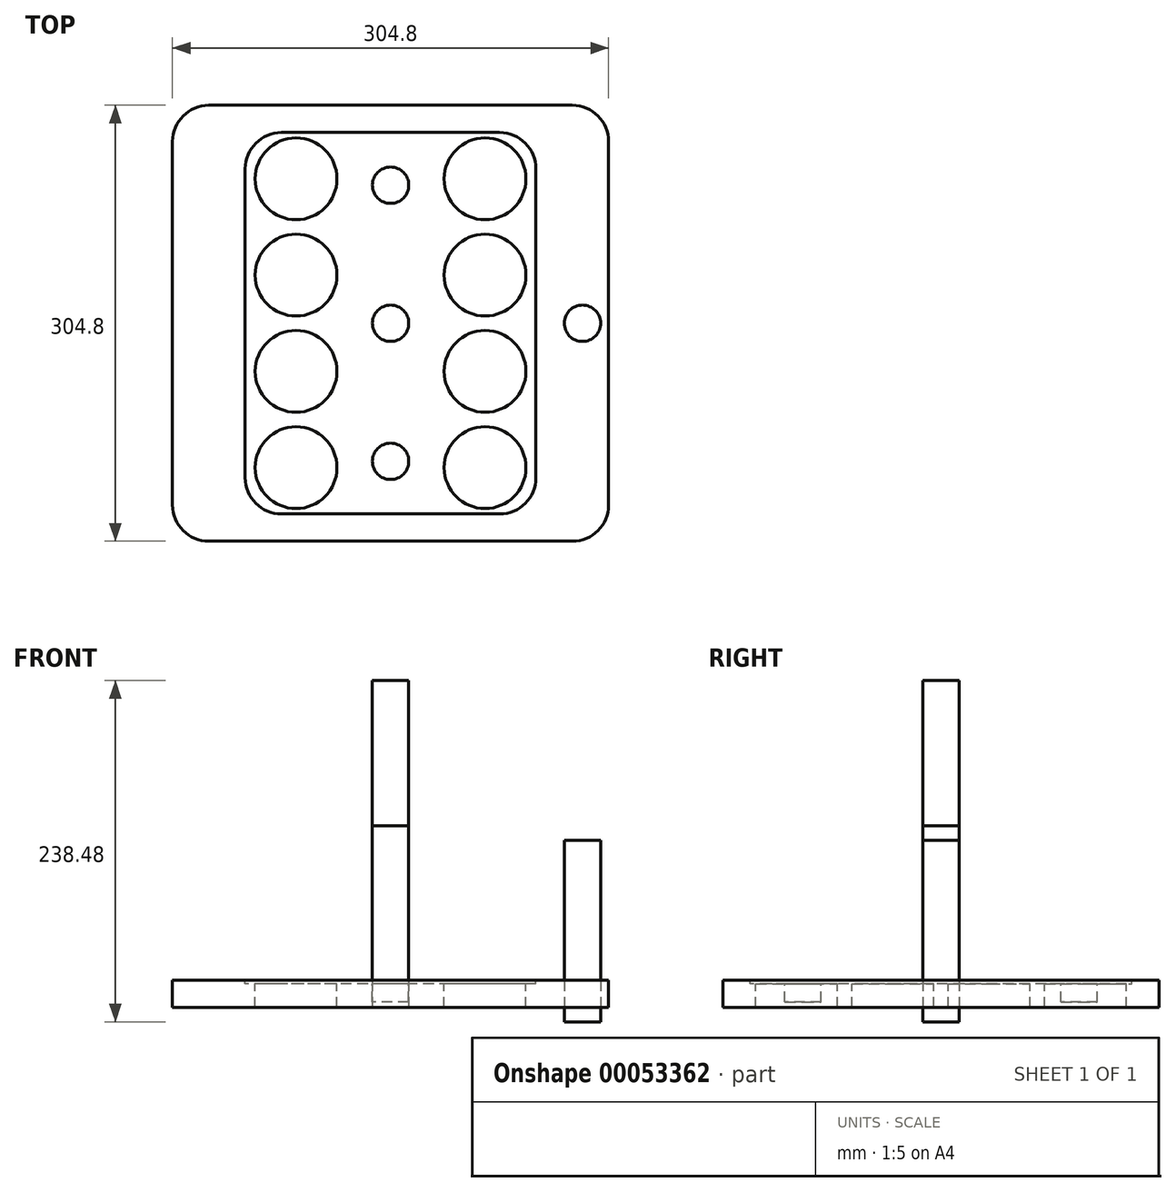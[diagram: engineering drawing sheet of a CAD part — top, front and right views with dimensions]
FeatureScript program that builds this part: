
annotation { "Feature Type Name" : "Feature", "Feature Type Description" : "" }
export const myFeature = defineFeature(function(context is Context, id is Id, definition is map)
    precondition{}
    {
        {
            var Q0;
            Q0=qCreatedBy(makeId("Top.planeOp"),FACE);
            var sketch = newSketch(context, id + "F0", { "sketchPlane" : qUnion([Q0])});
            skLineSegment(sketch, "E0.rect.bottom", {"start": v(127, 152.4) * mm, "end": v(-127, 152.4) * mm});
            skLineSegment(sketch, "E0.rect.top", {"start": v(127, -152.4) * mm, "end": v(-127, -152.4) * mm});
            skLineSegment(sketch, "E0.rect.left", {"start": v(152.4, 127) * mm, "end": v(152.4, -127) * mm});
            skLineSegment(sketch, "E0.rect.right", {"start": v(-152.4, 127) * mm, "end": v(-152.4, -127) * mm});
            skPoint(sketch, "E1.visualSharp", {"position": v(-152.4, 152.4) * mm});
            skArc(sketch, "E1.filletArc", {"start": v(-127, 152.4) * mm, "mid": v(-144.96, 144.96) * mm, "end": v(-152.4, 127) * mm});
            skPoint(sketch, "E2.visualSharp", {"position": v(152.4, 152.4) * mm});
            skArc(sketch, "E2.filletArc", {"start": v(152.4, 127) * mm, "mid": v(144.96, 144.96) * mm, "end": v(127, 152.4) * mm});
            skPoint(sketch, "E3.visualSharp", {"position": v(152.4, -152.4) * mm});
            skArc(sketch, "E3.filletArc", {"start": v(127, -152.4) * mm, "mid": v(144.96, -144.96) * mm, "end": v(152.4, -127) * mm});
            skPoint(sketch, "E4.visualSharp", {"position": v(-152.4, -152.4) * mm});
            skArc(sketch, "E4.filletArc", {"start": v(-152.4, -127) * mm, "mid": v(-144.96, -144.96) * mm, "end": v(-127, -152.4) * mm});
            skSolve(sketch);
        }
        {
            var Q0;
            Q0=qSketchRegion(id+"F0",true);
            extrude(context, id + "F1", {"entities" : qUnion([Q0]), "depth" : 19.05 * mm});
        }
        {
            var Q0;
            Q0=makeQuery(id+"F1.opExtrude","CAP_FACE",FACE,{"disambiguationData":[OSD([sQuery(id+"F0.wireOp",EDGE,"E0.rect.bottom"),sQuery(id+"F0.wireOp",EDGE,"E0.rect.top"),sQuery(id+"F0.wireOp",EDGE,"E0.rect.left"),sQuery(id+"F0.wireOp",EDGE,"E0.rect.right"),sQuery(id+"F0.wireOp",EDGE,"E1.filletArc"),sQuery(id+"F0.wireOp",EDGE,"E2.filletArc"),sQuery(id+"F0.wireOp",EDGE,"E3.filletArc"),sQuery(id+"F0.wireOp",EDGE,"E4.filletArc")])],"isStart":false});
            var sketch = newSketch(context, id + "F2", { "sketchPlane" : qUnion([Q0])});
            skCircle(sketch, "E5", {"center": v(-66.04, 100.96) * mm, "radius": 28.58 * mm});
            skCircle(sketch, "E6", {"center": v(-66.04, 33.65) * mm, "radius": 28.58 * mm});
            skCircle(sketch, "E7", {"center": v(-66.04, -33.66) * mm, "radius": 28.58 * mm});
            skCircle(sketch, "E8", {"center": v(-66.04, -100.97) * mm, "radius": 28.58 * mm});
            skLineSegment(sketch, "E9", {"start": v(-211.39, 0) * mm, "end": v(197.24, 0) * mm, "construction": true});
            skPoint(sketch, "E9.endSnap0", {"position": v(-152.4, 0) * mm});
            skCircle(sketch, "E10.MirrorC", {"center": v(66.04, -100.97) * mm, "radius": 28.58 * mm});
            skCircle(sketch, "E11.MirrorC", {"center": v(66.04, -33.66) * mm, "radius": 28.58 * mm});
            skCircle(sketch, "E12.MirrorC", {"center": v(66.04, 33.65) * mm, "radius": 28.58 * mm});
            skCircle(sketch, "E13.MirrorC", {"center": v(66.04, 100.96) * mm, "radius": 28.58 * mm});
            skSolve(sketch);
        }
        {
            var Q0;
            Q0=qSketchRegion(id+"F2",true);
            extrude(context, id + "F3", {"entities" : qUnion([Q0]), "operationType" : NewBodyOperationType.REMOVE, "endBound" : BoundingType.THROUGH_ALL, "oppositeDirection" : true, "depth" : 25.4 * mm});
        }
        {
            var Q0;
            Q0=makeQuery(id+"F1.opExtrude","CAP_FACE",FACE,{"disambiguationData":[OSD([sQuery(id+"F0.wireOp",EDGE,"E0.rect.bottom"),sQuery(id+"F0.wireOp",EDGE,"E0.rect.top"),sQuery(id+"F0.wireOp",EDGE,"E0.rect.left"),sQuery(id+"F0.wireOp",EDGE,"E0.rect.right"),sQuery(id+"F0.wireOp",EDGE,"E1.filletArc"),sQuery(id+"F0.wireOp",EDGE,"E2.filletArc"),sQuery(id+"F0.wireOp",EDGE,"E3.filletArc"),sQuery(id+"F0.wireOp",EDGE,"E4.filletArc")])],"isStart":false});
            var sketch = newSketch(context, id + "F4", { "sketchPlane" : qUnion([Q0])});
            skCircle(sketch, "E14", {"center": v(0, 96.52) * mm, "radius": 12.7 * mm});
            skCircle(sketch, "E15.MirrorC", {"center": v(0, -96.52) * mm, "radius": 12.7 * mm});
            skSolve(sketch);
        }
        {
            var Q0;
            Q0=qSketchRegion(id+"F4",true);
            extrude(context, id + "F5", {"entities" : qUnion([Q0]), "operationType" : NewBodyOperationType.REMOVE, "oppositeDirection" : true, "depth" : 15.24 * mm});
        }
        {
            var Q0;
            Q0=makeQuery(id+"F1.opExtrude","CAP_FACE",FACE,{"disambiguationData":[OSD([sQuery(id+"F0.wireOp",EDGE,"E0.rect.bottom"),sQuery(id+"F0.wireOp",EDGE,"E0.rect.top"),sQuery(id+"F0.wireOp",EDGE,"E0.rect.left"),sQuery(id+"F0.wireOp",EDGE,"E0.rect.right"),sQuery(id+"F0.wireOp",EDGE,"E1.filletArc"),sQuery(id+"F0.wireOp",EDGE,"E2.filletArc"),sQuery(id+"F0.wireOp",EDGE,"E3.filletArc"),sQuery(id+"F0.wireOp",EDGE,"E4.filletArc")])],"isStart":false});
            var sketch = newSketch(context, id + "F6", { "sketchPlane" : qUnion([Q0])});
            skLineSegment(sketch, "E16.rect.bottom", {"start": v(76.2, 133.35) * mm, "end": v(-76.2, 133.35) * mm});
            skLineSegment(sketch, "E16.rect.top", {"start": v(76.2, -133.35) * mm, "end": v(-76.2, -133.35) * mm});
            skLineSegment(sketch, "E16.rect.left", {"start": v(101.6, 107.95) * mm, "end": v(101.6, -107.95) * mm});
            skLineSegment(sketch, "E16.rect.right", {"start": v(-101.6, 107.95) * mm, "end": v(-101.6, -107.95) * mm});
            skPoint(sketch, "E16.rect.middle", {"position": v(0, 0) * mm});
            skPoint(sketch, "E17.visualSharp", {"position": v(-101.6, 133.35) * mm});
            skArc(sketch, "E17.filletArc", {"start": v(-76.2, 133.35) * mm, "mid": v(-94.16, 125.91) * mm, "end": v(-101.6, 107.95) * mm});
            skPoint(sketch, "E18.visualSharp", {"position": v(101.6, 133.35) * mm});
            skArc(sketch, "E18.filletArc", {"start": v(101.6, 107.95) * mm, "mid": v(94.16, 125.91) * mm, "end": v(76.2, 133.35) * mm});
            skPoint(sketch, "E19.visualSharp", {"position": v(101.6, -133.35) * mm});
            skArc(sketch, "E19.filletArc", {"start": v(76.2, -133.35) * mm, "mid": v(94.16, -125.91) * mm, "end": v(101.6, -107.95) * mm});
            skPoint(sketch, "E20.visualSharp", {"position": v(-101.6, -133.35) * mm});
            skArc(sketch, "E20.filletArc", {"start": v(-101.6, -107.95) * mm, "mid": v(-94.16, -125.91) * mm, "end": v(-76.2, -133.35) * mm});
            skSolve(sketch);
        }
        {
            var Q0;
            Q0=makeQuery(id+"F6.imprint","IMPRINT",FACE,{"disambiguationData":[TD([[makeQuery(id+"F6.imprint","IMPRINT",EDGE,{"derivedFrom":sQuery(id+"F6.wireOp",EDGE,"E16.rect.bottom")}),1.0]])]});
            extrude(context, id + "F7", {"entities" : qUnion([Q0]), "operationType" : NewBodyOperationType.REMOVE, "oppositeDirection" : true, "depth" : 2.54 * mm});
        }
        {
            var Q0;
            Q0=qCreatedBy(makeId("Top.planeOp"),FACE);
            var sketch = newSketch(context, id + "F8", { "sketchPlane" : qUnion([Q0])});
            skCircle(sketch, "E21", {"center": v(0, 0) * mm, "radius": 12.7 * mm});
            skSolve(sketch);
        }
        {
            var Q0;
            Q0 = qSketchRegion(id + "F8", true);
            extrude(context, id + "F9", {"entities" : qUnion([Q0]), "depth" : 127 * mm});
        }
        {
            var Q0;
            Q0=makeQuery(id+"F9.opExtrude","SWEPT_BODY",BODY,{"disambiguationData":[OSD([sQuery(id+"F8.wireOp",EDGE,"E21")])]});
            transform(context, id + "F10", {"entities" : qUnion([Q0]), "transformType" : TransformType.TRANSLATION_3D, "dx" : 134.07 * mm, "dy" : 0 * mm, "dz" : -9.88 * mm, "makeCopy" : true});
        }
        {
            var Q0;
            Q0=qCreatedBy(makeId("Top.planeOp"),FACE);
            var sketch = newSketch(context, id + "F11", { "sketchPlane" : qUnion([Q0])});
            skCircle(sketch, "E22", {"center": v(0, 0) * mm, "radius": 12.7 * mm});
            skSolve(sketch);
        }
        {
            var Q0;
            Q0 = qSketchRegion(id + "F11", true);
            extrude(context, id + "F12", {"entities" : qUnion([Q0]), "depth" : 228.6 * mm});
        }
    });
